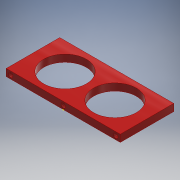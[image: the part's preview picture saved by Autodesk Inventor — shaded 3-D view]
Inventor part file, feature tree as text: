
AUTODESK INVENTOR PART (.ipt)
format: ipt  version: 2019.3 (Build 233278000, 278)  size: 123,904 bytes
history: native  units: mm
features: sketch x4, hole x2, extrude x1, projected_geometry x1
ambient origin geometry x8: Origin, YZ Plane, XZ Plane, XY Plane, X Axis, Y Axis, Z Axis, Center Point
bodies: Solid1 (feature_tree)
feature tree (8):
  extrude  "Extrusion1"  Depth=60.0mm
  hole  "Hole1"  [1 undecoded]
  sketch  "Sketch3"  dims[d5=5.0mm]
  hole  "Hole2"  [1 undecoded]
  sketch  "Sketch1"  dims[d0=128.0mm d1=60.0mm]
  sketch  "Sketch2"  dims[d2=8.0mm d3=0.0mm d4=5.0mm]
  projected_geometry  "Projected Loop1"
  sketch  "Sketch4"  dims[d6=5.0mm d7=6.0mm d8=4.0mm d9=2.0mm d10=90.0deg d11=8.0mm d12=20.594885mm d13=48.0mm d14=6.0mm d15=4.0mm d16=2.0mm d17=90.0deg d18=8.0mm d19=20.594885mm]
note: 2 required parameter values undecoded (feature->parameter linkage not recoverable at this tier; creation-order binding heuristic only, values carry confidence <= 0.55)
